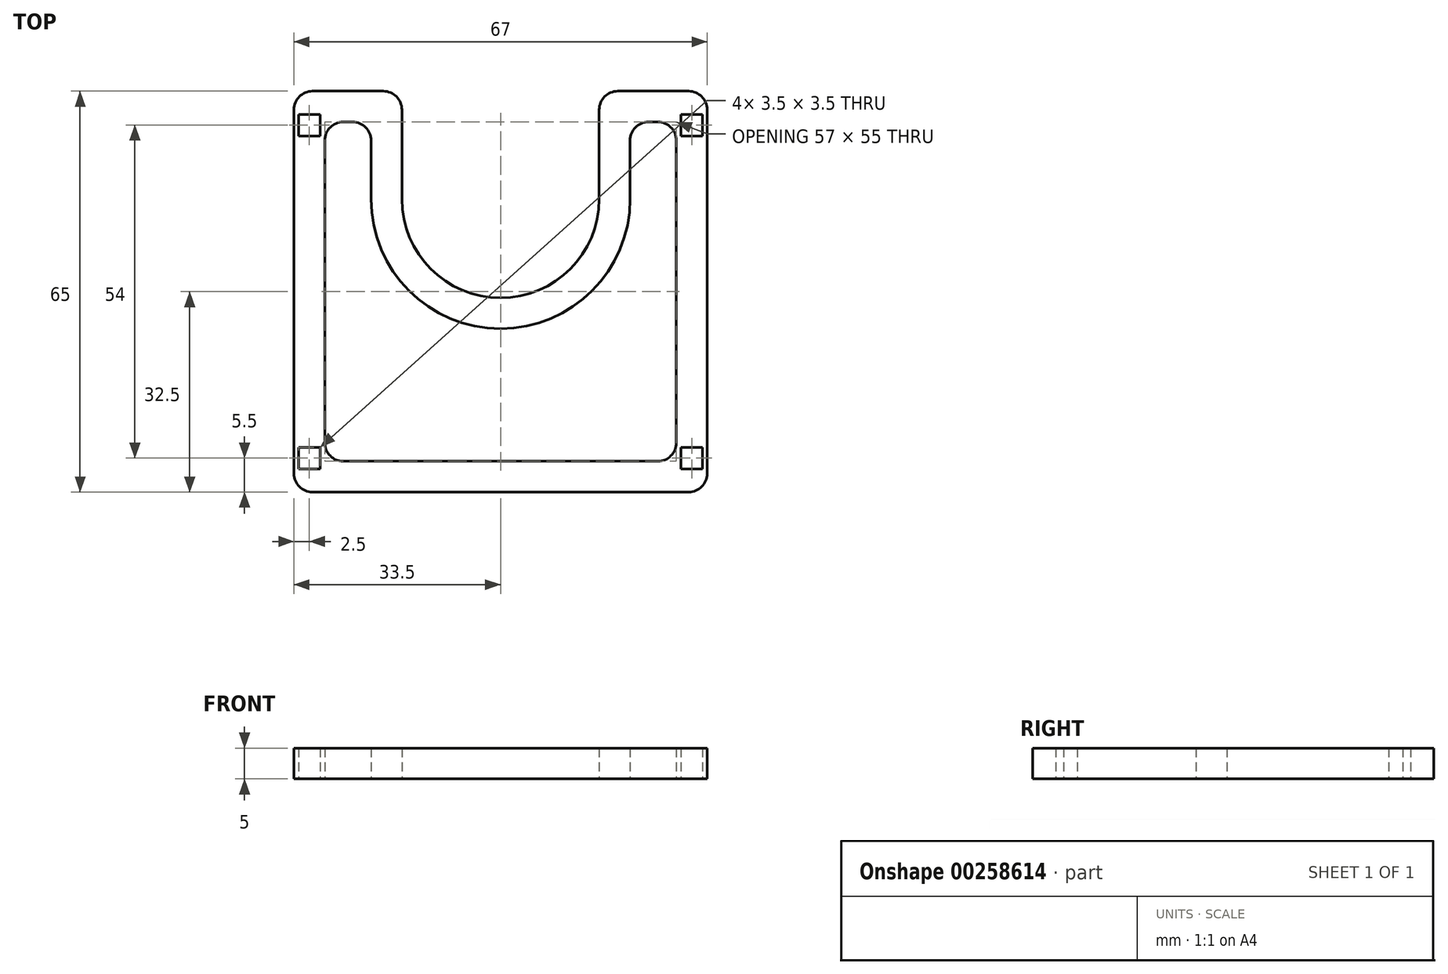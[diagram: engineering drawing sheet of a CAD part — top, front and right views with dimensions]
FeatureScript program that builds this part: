
annotation { "Feature Type Name" : "Feature", "Feature Type Description" : "" }
export const myFeature = defineFeature(function(context is Context, id is Id, definition is map)
    precondition{}
    {
        {
            var Q0;
            Q0=qCreatedBy(makeId("Top.planeOp"),FACE);
            var sketch = newSketch(context, id + "F0", { "sketchPlane" : qUnion([Q0])});
            skLineSegment(sketch, "E0.bottom", {"start": v(33.5, 32.5) * mm, "end": v(-33.5, 32.5) * mm});
            skLineSegment(sketch, "E0.top", {"start": v(33.5, -32.5) * mm, "end": v(-33.5, -32.5) * mm});
            skLineSegment(sketch, "E0.left", {"start": v(33.5, 32.5) * mm, "end": v(33.5, -32.5) * mm});
            skLineSegment(sketch, "E0.right", {"start": v(-33.5, 32.5) * mm, "end": v(-33.5, -32.5) * mm});
            skPoint(sketch, "E0.middle", {"position": v(0, 0) * mm});
            skLineSegment(sketch, "E1.bottom", {"start": v(-33.5, 32.5) * mm, "end": v(-28.5, 32.5) * mm, "construction": true});
            skLineSegment(sketch, "E1.top", {"start": v(-33.5, 29.5) * mm, "end": v(-28.5, 29.5) * mm, "construction": true});
            skLineSegment(sketch, "E1.left", {"start": v(-33.5, 32.5) * mm, "end": v(-33.5, 29.5) * mm, "construction": true});
            skLineSegment(sketch, "E1.right", {"start": v(-28.5, 32.5) * mm, "end": v(-28.5, 29.5) * mm, "construction": true});
            skLineSegment(sketch, "E2.bottom", {"start": v(33.5, 32.5) * mm, "end": v(28.5, 32.5) * mm, "construction": true});
            skLineSegment(sketch, "E2.top", {"start": v(33.5, 29.5) * mm, "end": v(28.5, 29.5) * mm, "construction": true});
            skLineSegment(sketch, "E2.left", {"start": v(33.5, 32.5) * mm, "end": v(33.5, 29.5) * mm, "construction": true});
            skLineSegment(sketch, "E2.right", {"start": v(28.5, 32.5) * mm, "end": v(28.5, 29.5) * mm, "construction": true});
            skLineSegment(sketch, "E3.bottom", {"start": v(33.5, -32.5) * mm, "end": v(28.5, -32.5) * mm, "construction": true});
            skLineSegment(sketch, "E3.top", {"start": v(33.5, -29.5) * mm, "end": v(28.5, -29.5) * mm, "construction": true});
            skLineSegment(sketch, "E3.left", {"start": v(33.5, -32.5) * mm, "end": v(33.5, -29.5) * mm, "construction": true});
            skLineSegment(sketch, "E3.right", {"start": v(28.5, -32.5) * mm, "end": v(28.5, -29.5) * mm, "construction": true});
            skLineSegment(sketch, "E4.bottom", {"start": v(-33.5, -32.5) * mm, "end": v(-28.5, -32.5) * mm, "construction": true});
            skLineSegment(sketch, "E4.top", {"start": v(-33.5, -29.5) * mm, "end": v(-28.5, -29.5) * mm, "construction": true});
            skLineSegment(sketch, "E4.left", {"start": v(-33.5, -32.5) * mm, "end": v(-33.5, -29.5) * mm, "construction": true});
            skLineSegment(sketch, "E4.right", {"start": v(-28.5, -32.5) * mm, "end": v(-28.5, -29.5) * mm, "construction": true});
            skLineSegment(sketch, "E5.top", {"start": v(-33.5, 24.5) * mm, "end": v(-28.5, 24.5) * mm, "construction": true});
            skLineSegment(sketch, "E5.left", {"start": v(-33.5, 29.5) * mm, "end": v(-33.5, 24.5) * mm, "construction": true});
            skLineSegment(sketch, "E5.right", {"start": v(-28.5, 29.5) * mm, "end": v(-28.5, 24.5) * mm, "construction": true});
            skLineSegment(sketch, "E6.top", {"start": v(33.5, 24.5) * mm, "end": v(28.5, 24.5) * mm, "construction": true});
            skLineSegment(sketch, "E6.left", {"start": v(33.5, 29.5) * mm, "end": v(33.5, 24.5) * mm, "construction": true});
            skLineSegment(sketch, "E6.right", {"start": v(28.5, 29.5) * mm, "end": v(28.5, 24.5) * mm, "construction": true});
            skLineSegment(sketch, "E7.top", {"start": v(33.5, -24.5) * mm, "end": v(28.5, -24.5) * mm, "construction": true});
            skLineSegment(sketch, "E7.left", {"start": v(33.5, -29.5) * mm, "end": v(33.5, -24.5) * mm, "construction": true});
            skLineSegment(sketch, "E7.right", {"start": v(28.5, -29.5) * mm, "end": v(28.5, -24.5) * mm, "construction": true});
            skLineSegment(sketch, "E8.top", {"start": v(-33.5, -24.5) * mm, "end": v(-28.5, -24.5) * mm, "construction": true});
            skLineSegment(sketch, "E8.left", {"start": v(-33.5, -29.5) * mm, "end": v(-33.5, -24.5) * mm, "construction": true});
            skLineSegment(sketch, "E8.right", {"start": v(-28.5, -29.5) * mm, "end": v(-28.5, -24.5) * mm, "construction": true});
            skLineSegment(sketch, "E9.bottom", {"start": v(-32.75, -28.75) * mm, "end": v(-29.25, -28.75) * mm});
            skLineSegment(sketch, "E9.top", {"start": v(-32.75, -25.25) * mm, "end": v(-29.25, -25.25) * mm});
            skLineSegment(sketch, "E9.left", {"start": v(-32.75, -28.75) * mm, "end": v(-32.75, -25.25) * mm});
            skLineSegment(sketch, "E9.right", {"start": v(-29.25, -28.75) * mm, "end": v(-29.25, -25.25) * mm});
            skPoint(sketch, "E9.middle", {"position": v(-31, -27) * mm});
            skPoint(sketch, "E9.middle.positionSnap0", {"position": v(-31, -24.5) * mm});
            skPoint(sketch, "E9.middle.positionSnap1", {"position": v(-28.5, -27) * mm});
            skPoint(sketch, "E9.centerSnap0", {"position": v(-31, -24.5) * mm});
            skPoint(sketch, "E9.centerSnap1", {"position": v(-28.5, -27) * mm});
            skLineSegment(sketch, "E10.bottom", {"start": v(32.75, -28.75) * mm, "end": v(29.25, -28.75) * mm});
            skLineSegment(sketch, "E10.top", {"start": v(32.75, -25.25) * mm, "end": v(29.25, -25.25) * mm});
            skLineSegment(sketch, "E10.left", {"start": v(32.75, -28.75) * mm, "end": v(32.75, -25.25) * mm});
            skLineSegment(sketch, "E10.right", {"start": v(29.25, -28.75) * mm, "end": v(29.25, -25.25) * mm});
            skPoint(sketch, "E10.middle", {"position": v(31, -27) * mm});
            skPoint(sketch, "E10.middle.positionSnap0", {"position": v(28.5, -27) * mm});
            skPoint(sketch, "E10.middle.positionSnap1", {"position": v(31, -24.5) * mm});
            skPoint(sketch, "E10.centerSnap0", {"position": v(28.5, -27) * mm});
            skPoint(sketch, "E10.centerSnap1", {"position": v(31, -24.5) * mm});
            skLineSegment(sketch, "E11.bottom", {"start": v(-29.25, 25.25) * mm, "end": v(-32.75, 25.25) * mm});
            skLineSegment(sketch, "E11.top", {"start": v(-29.25, 28.75) * mm, "end": v(-32.75, 28.75) * mm});
            skLineSegment(sketch, "E11.left", {"start": v(-29.25, 25.25) * mm, "end": v(-29.25, 28.75) * mm});
            skLineSegment(sketch, "E11.right", {"start": v(-32.75, 25.25) * mm, "end": v(-32.75, 28.75) * mm});
            skPoint(sketch, "E11.middle", {"position": v(-31, 27) * mm});
            skPoint(sketch, "E11.middle.positionSnap0", {"position": v(-33.5, 27) * mm});
            skPoint(sketch, "E11.middle.positionSnap1", {"position": v(-31, 29.5) * mm});
            skPoint(sketch, "E11.centerSnap0", {"position": v(-33.5, 27) * mm});
            skPoint(sketch, "E11.centerSnap1", {"position": v(-31, 29.5) * mm});
            skLineSegment(sketch, "E12.bottom", {"start": v(32.75, 25.25) * mm, "end": v(29.25, 25.25) * mm});
            skLineSegment(sketch, "E12.top", {"start": v(32.75, 28.75) * mm, "end": v(29.25, 28.75) * mm});
            skLineSegment(sketch, "E12.left", {"start": v(32.75, 25.25) * mm, "end": v(32.75, 28.75) * mm});
            skLineSegment(sketch, "E12.right", {"start": v(29.25, 25.25) * mm, "end": v(29.25, 28.75) * mm});
            skPoint(sketch, "E12.middle", {"position": v(31, 27) * mm});
            skPoint(sketch, "E12.middle.positionSnap0", {"position": v(28.5, 27) * mm});
            skPoint(sketch, "E12.middle.positionSnap1", {"position": v(31, 29.5) * mm});
            skPoint(sketch, "E12.centerSnap0", {"position": v(28.5, 27) * mm});
            skPoint(sketch, "E12.centerSnap1", {"position": v(31, 29.5) * mm});
            skLineSegment(sketch, "E13", {"start": v(0, 32.5) * mm, "end": v(0, -1) * mm, "construction": true});
            skPoint(sketch, "E13.endSnap0", {"position": v(0, 32.5) * mm});
            skLineSegment(sketch, "E14.bottom", {"start": v(16, 15) * mm, "end": v(-16, 15) * mm, "construction": true});
            skLineSegment(sketch, "E14.top", {"start": v(16, 50) * mm, "end": v(-16, 50) * mm, "construction": true});
            skLineSegment(sketch, "E14.left", {"start": v(16, 15) * mm, "end": v(16, 50) * mm, "construction": true});
            skLineSegment(sketch, "E14.right", {"start": v(-16, 15) * mm, "end": v(-16, 50) * mm, "construction": true});
            skLineSegment(sketch, "E15.bottom", {"start": v(-16, 32.5) * mm, "end": v(16, 32.5) * mm});
            skLineSegment(sketch, "E15.top", {"start": v(-16, 15) * mm, "end": v(16, 15) * mm});
            skLineSegment(sketch, "E15.left", {"start": v(-16, 32.5) * mm, "end": v(-16, 15) * mm});
            skLineSegment(sketch, "E15.right", {"start": v(16, 32.5) * mm, "end": v(16, 15) * mm});
            skArc(sketch, "E16", {"start": v(-16, 15) * mm, "mid": v(0, -1) * mm, "end": v(16, 15) * mm});
            skArc(sketch, "E17.0", {"start": v(-21, 15) * mm, "mid": v(0, -6) * mm, "end": v(21, 15) * mm});
            skLineSegment(sketch, "E18.bottom", {"start": v(-21, 15) * mm, "end": v(-16, 15) * mm});
            skLineSegment(sketch, "E18.top", {"start": v(-21, 27.5) * mm, "end": v(-16, 27.5) * mm});
            skLineSegment(sketch, "E18.left", {"start": v(-21, 15) * mm, "end": v(-21, 27.5) * mm});
            skLineSegment(sketch, "E18.right", {"start": v(-16, 15) * mm, "end": v(-16, 27.5) * mm});
            skLineSegment(sketch, "E19.bottom", {"start": v(21, 15) * mm, "end": v(16, 15) * mm});
            skLineSegment(sketch, "E19.top", {"start": v(21, 27.5) * mm, "end": v(16, 27.5) * mm});
            skLineSegment(sketch, "E19.left", {"start": v(21, 15) * mm, "end": v(21, 27.5) * mm});
            skLineSegment(sketch, "E19.right", {"start": v(16, 15) * mm, "end": v(16, 27.5) * mm});
            skLineSegment(sketch, "E20.bottom", {"start": v(28.5, 27.5) * mm, "end": v(-28.5, 27.5) * mm});
            skLineSegment(sketch, "E20.top", {"start": v(28.5, -27.5) * mm, "end": v(-28.5, -27.5) * mm});
            skLineSegment(sketch, "E20.left", {"start": v(28.5, 27.5) * mm, "end": v(28.5, -27.5) * mm});
            skLineSegment(sketch, "E20.right", {"start": v(-28.5, 27.5) * mm, "end": v(-28.5, -27.5) * mm});
            skSolve(sketch);
        }
        {
            var Q0;
            Q0=makeQuery(id+"F0.imprint","IMPRINT",FACE,{"disambiguationData":[TD([[makeQuery(id+"F0.imprint","IMPRINT",EDGE,{"derivedFrom":sQuery(id+"F0.wireOp",EDGE,"E0.top")}),-1.0]])]});
            var Q1;
            Q1=makeQuery(id+"F0.imprint","IMPRINT",FACE,{"disambiguationData":[TD([[makeQuery(id+"F0.imprint","IMPRINT",EDGE,{"derivedFrom":sQuery(id+"F0.wireOp",EDGE,"E18.bottom")}),1.0]])]});
            var Q2;
            Q2=makeQuery(id+"F0.imprint","IMPRINT",FACE,{"disambiguationData":[TD([[makeQuery(id+"F0.imprint","IMPRINT",EDGE,{"derivedFrom":sQuery(id+"F0.wireOp",EDGE,"E16")}),-1.0]])]});
            var Q3;
            Q3=makeQuery(id+"F0.imprint","IMPRINT",FACE,{"disambiguationData":[TD([[makeQuery(id+"F0.imprint","IMPRINT",EDGE,{"derivedFrom":sQuery(id+"F0.wireOp",EDGE,"E19.bottom")}),-1.0]])]});
            extrude(context, id + "F1", {"entities" : qUnion([Q0, Q1, Q2, Q3]), "depth" : 5 * mm});
        }
        {
            var Q0;
            Q0=makeQuery(id+"F1.opExtrude","SWEPT_EDGE",EDGE,{"disambiguationData":[OSD([sQuery(id+"F0.wireOp",EDGE,"E0.bottom"),sQuery(id+"F0.wireOp",EDGE,"E0.right")])]});
            var Q1;
            Q1=makeQuery(id+"F1.opExtrude","SWEPT_EDGE",EDGE,{"disambiguationData":[OSD([sQuery(id+"F0.wireOp",EDGE,"E0.bottom"),sQuery(id+"F0.wireOp",EDGE,"E15.bottom"),sQuery(id+"F0.wireOp",EDGE,"E15.left")])]});
            var Q2;
            Q2=makeQuery(id+"F1.opExtrude","SWEPT_EDGE",EDGE,{"disambiguationData":[OSD([sQuery(id+"F0.wireOp",EDGE,"E0.bottom"),sQuery(id+"F0.wireOp",EDGE,"E15.bottom"),sQuery(id+"F0.wireOp",EDGE,"E15.right")])]});
            var Q3;
            Q3=makeQuery(id+"F1.opExtrude","SWEPT_EDGE",EDGE,{"disambiguationData":[OSD([sQuery(id+"F0.wireOp",EDGE,"E0.bottom"),sQuery(id+"F0.wireOp",EDGE,"E0.left")])]});
            var Q4;
            Q4=makeQuery(id+"F1.opExtrude","SWEPT_EDGE",EDGE,{"disambiguationData":[OSD([sQuery(id+"F0.wireOp",EDGE,"E20.bottom"),sQuery(id+"F0.wireOp",EDGE,"E20.right")])]});
            var Q5;
            Q5=makeQuery(id+"F1.opExtrude","SWEPT_EDGE",EDGE,{"disambiguationData":[OSD([sQuery(id+"F0.wireOp",EDGE,"E18.left"),sQuery(id+"F0.wireOp",EDGE,"E20.bottom")])]});
            var Q6;
            Q6=makeQuery(id+"F1.opExtrude","SWEPT_EDGE",EDGE,{"disambiguationData":[OSD([sQuery(id+"F0.wireOp",EDGE,"E19.left"),sQuery(id+"F0.wireOp",EDGE,"E20.bottom")])]});
            var Q7;
            Q7=makeQuery(id+"F1.opExtrude","SWEPT_EDGE",EDGE,{"disambiguationData":[OSD([sQuery(id+"F0.wireOp",EDGE,"E20.bottom"),sQuery(id+"F0.wireOp",EDGE,"E20.left")])]});
            var Q8;
            Q8=makeQuery(id+"F1.opExtrude","SWEPT_EDGE",EDGE,{"disambiguationData":[OSD([sQuery(id+"F0.wireOp",EDGE,"E20.top"),sQuery(id+"F0.wireOp",EDGE,"E20.left")])]});
            var Q9;
            Q9=makeQuery(id+"F1.opExtrude","SWEPT_EDGE",EDGE,{"disambiguationData":[OSD([sQuery(id+"F0.wireOp",EDGE,"E20.top"),sQuery(id+"F0.wireOp",EDGE,"E20.right")])]});
            var Q10;
            Q10=makeQuery(id+"F1.opExtrude","SWEPT_EDGE",EDGE,{"disambiguationData":[OSD([sQuery(id+"F0.wireOp",EDGE,"E0.top"),sQuery(id+"F0.wireOp",EDGE,"E0.left")])]});
            var Q11;
            Q11=makeQuery(id+"F1.opExtrude","SWEPT_EDGE",EDGE,{"disambiguationData":[OSD([sQuery(id+"F0.wireOp",EDGE,"E0.top"),sQuery(id+"F0.wireOp",EDGE,"E0.right")])]});
            fillet(context, id + "F2", {"entities" : qUnion([Q0, Q1, Q2, Q3, Q4, Q5, Q6, Q7, Q8, Q9, Q10, Q11]), "radius" : 3 * mm, "tangentPropagation" : true, "allowEdgeOverflow" : false});
        }
    });
